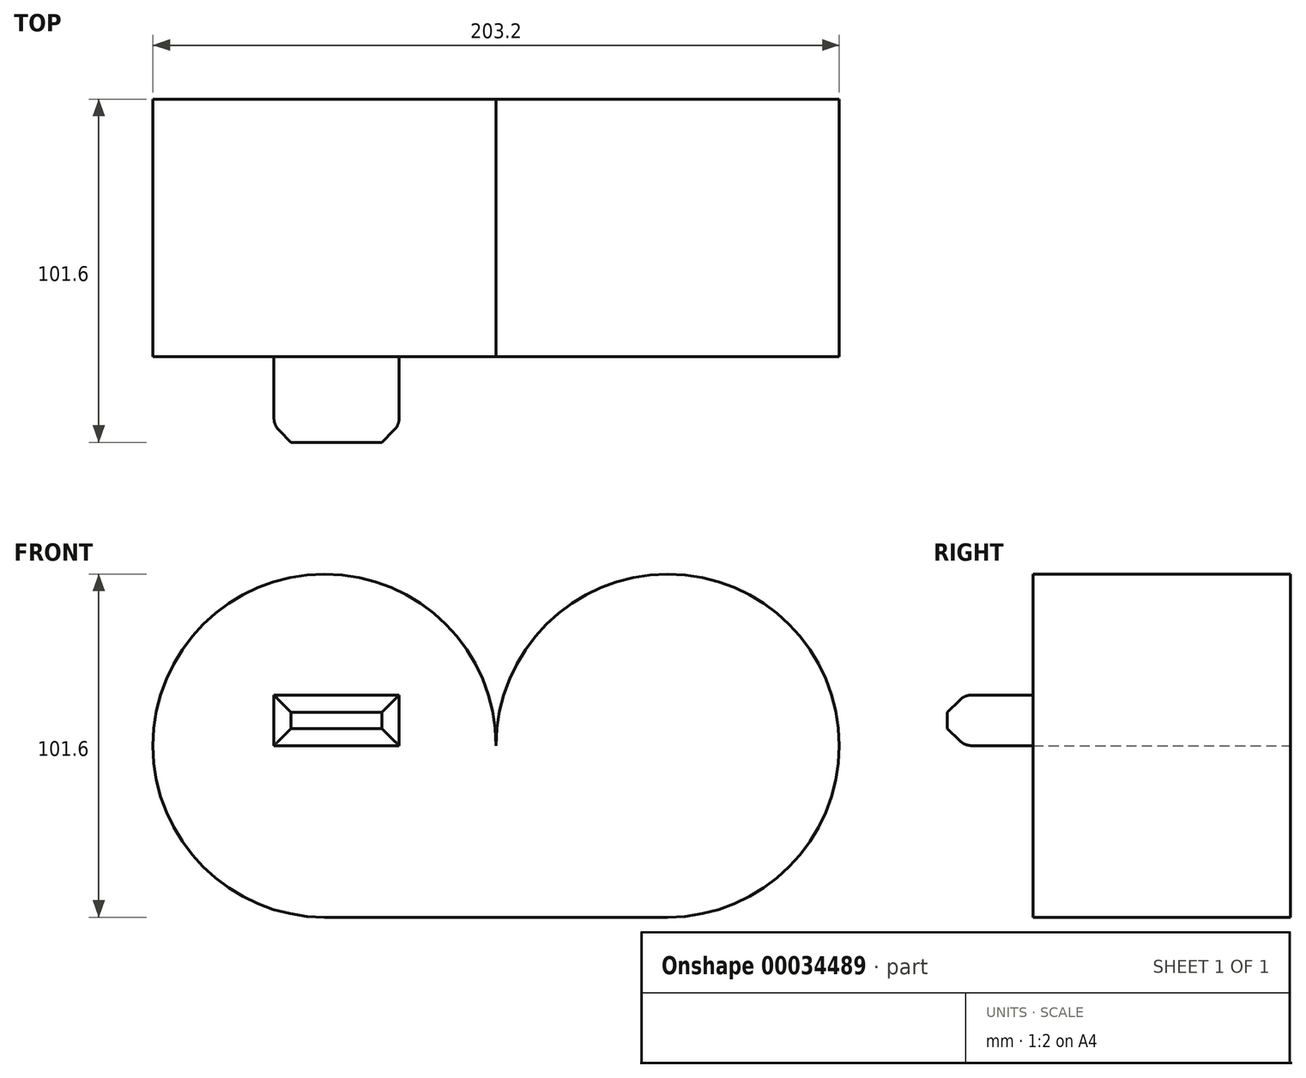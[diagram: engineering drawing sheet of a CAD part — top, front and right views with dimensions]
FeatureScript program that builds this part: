
annotation { "Feature Type Name" : "Feature", "Feature Type Description" : "" }
export const myFeature = defineFeature(function(context is Context, id is Id, definition is map)
    precondition{}
    {
        {
            var Q0;
            Q0=qCreatedBy(makeId("Front.planeOp"),FACE);
            var sketch = newSketch(context, id + "F0", { "sketchPlane" : qUnion([Q0])});
            skLineSegment(sketch, "E0.top", {"start": v(-50.8, -50.8) * mm, "end": v(50.8, -50.8) * mm});
            skLineSegment(sketch, "E0.left", {"start": v(-50.8, -50.8) * mm, "end": v(-50.8, -50.8) * mm});
            skLineSegment(sketch, "E0.right", {"start": v(50.8, -50.8) * mm, "end": v(50.8, -50.8) * mm});
            skArc(sketch, "E1", {"start": v(0, 0) * mm, "mid": v(-86.72, 35.92) * mm, "end": v(-50.8, -50.8) * mm});
            skArc(sketch, "E2", {"start": v(50.8, -50.8) * mm, "mid": v(86.72, 35.92) * mm, "end": v(0, 0) * mm});
            skSolve(sketch);
        }
        {
            var Q0;
            Q0 = qSketchRegion(id + "F0", true);
            extrude(context, id + "F1", {"entities" : qUnion([Q0]), "depth" : 76.2 * mm});
        }
        {
            var Q0;
            Q0=makeQuery(id+"F1.opExtrude","CAP_FACE",FACE,{"disambiguationData":[OSD([sQuery(id+"F0.wireOp",EDGE,"E0.top"),sQuery(id+"F0.wireOp",EDGE,"E1"),sQuery(id+"F0.wireOp",EDGE,"E2")])],"isStart":false});
            var sketch = newSketch(context, id + "F2", { "sketchPlane" : qUnion([Q0])});
            skLineSegment(sketch, "E3.bottom", {"start": v(-65.78, 14.95) * mm, "end": v(-28.7, 14.95) * mm});
            skLineSegment(sketch, "E3.top", {"start": v(-65.78, 0) * mm, "end": v(-28.7, 0) * mm});
            skLineSegment(sketch, "E3.left", {"start": v(-65.78, 14.95) * mm, "end": v(-65.78, 0) * mm});
            skLineSegment(sketch, "E3.right", {"start": v(-28.7, 14.95) * mm, "end": v(-28.7, 0) * mm});
            skSolve(sketch);
        }
        {
            var Q0;
            Q0 = qSketchRegion(id + "F2", true);
            extrude(context, id + "F3", {"entities" : qUnion([Q0]), "operationType" : NewBodyOperationType.ADD, "depth" : 25.4 * mm});
        }
        {
            var Q0;
            Q0=makeQuery(id+"F3.opExtrude","CAP_EDGE",EDGE,{"disambiguationData":[OSD([sQuery(id+"F2.wireOp",EDGE,"E3.bottom")])],"isStart":false});
            var Q1;
            Q1=makeQuery(id+"F3.opExtrude","CAP_EDGE",EDGE,{"disambiguationData":[OSD([sQuery(id+"F2.wireOp",EDGE,"E3.left")])],"isStart":false});
            var Q2;
            Q2=makeQuery(id+"F3.opExtrude","CAP_EDGE",EDGE,{"disambiguationData":[OSD([sQuery(id+"F2.wireOp",EDGE,"E3.top")])],"isStart":false});
            var Q3;
            Q3=makeQuery(id+"F3.opExtrude","CAP_EDGE",EDGE,{"disambiguationData":[OSD([sQuery(id+"F2.wireOp",EDGE,"E3.right")])],"isStart":false});
            chamfer(context, id + "F4", {"entities" : qUnion([Q0, Q1, Q2, Q3]), "width" : 5.08 * mm, "tangentPropagation" : true});
        }
        {
            var Q0;
            {var subQ0=sQuery(id+"F2.wireOp",EDGE,"E3.top");Q0=makeQuery(id+"F4.opChamfer","BLEND_EDGE",EDGE,{"blendedFrom":[makeQuery(id+"F3.opExtrude","CAP_EDGE",EDGE,{"disambiguationData":[OSD([subQ0])],"isStart":false}),makeQuery(id+"F3.opExtrude","SWEPT_FACE",FACE,{"disambiguationData":[OSD([subQ0])]})],"blendedInto":[makeQuery(id+"F3.opExtrude","SWEPT_FACE",FACE,{"disambiguationData":[OSD([subQ0])]})]});}
            var Q1;
            {var subQ0=sQuery(id+"F2.wireOp",EDGE,"E3.left");Q1=makeQuery(id+"F4.opChamfer","BLEND_EDGE",EDGE,{"blendedFrom":[makeQuery(id+"F3.opExtrude","CAP_EDGE",EDGE,{"disambiguationData":[OSD([subQ0])],"isStart":false}),makeQuery(id+"F3.opExtrude","SWEPT_FACE",FACE,{"disambiguationData":[OSD([subQ0])]})],"blendedInto":[makeQuery(id+"F3.opExtrude","SWEPT_FACE",FACE,{"disambiguationData":[OSD([subQ0])]})]});}
            var Q2;
            {var subQ0=sQuery(id+"F2.wireOp",EDGE,"E3.bottom");Q2=makeQuery(id+"F4.opChamfer","BLEND_EDGE",EDGE,{"blendedFrom":[makeQuery(id+"F3.opExtrude","CAP_EDGE",EDGE,{"disambiguationData":[OSD([subQ0])],"isStart":false}),makeQuery(id+"F3.opExtrude","SWEPT_FACE",FACE,{"disambiguationData":[OSD([subQ0])]})],"blendedInto":[makeQuery(id+"F3.opExtrude","SWEPT_FACE",FACE,{"disambiguationData":[OSD([subQ0])]})]});}
            var Q3;
            {var subQ0=sQuery(id+"F2.wireOp",EDGE,"E3.right");Q3=makeQuery(id+"F4.opChamfer","BLEND_EDGE",EDGE,{"blendedFrom":[makeQuery(id+"F3.opExtrude","CAP_EDGE",EDGE,{"disambiguationData":[OSD([subQ0])],"isStart":false}),makeQuery(id+"F3.opExtrude","SWEPT_FACE",FACE,{"disambiguationData":[OSD([subQ0])]})],"blendedInto":[makeQuery(id+"F3.opExtrude","SWEPT_FACE",FACE,{"disambiguationData":[OSD([subQ0])]})]});}
            fillet(context, id + "F5", {"entities" : qUnion([Q0, Q1, Q2, Q3]), "radius" : 5.08 * mm, "tangentPropagation" : true, "allowEdgeOverflow" : false});
        }
    });
